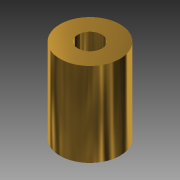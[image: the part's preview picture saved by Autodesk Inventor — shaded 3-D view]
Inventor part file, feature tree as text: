
AUTODESK INVENTOR PART (.ipt)
format: ipt  version: 2015 (Build 190159000, 159)  size: 105,984 bytes
history: native  units: mm
features: extrude x2, sketch x2, other x1
ambient origin geometry x8: Origin, YZ Plane, XZ Plane, XY Plane, X Axis, Y Axis, Z Axis, Center Point
bodies: Body1 (feature_tree)
feature tree (5):
  other  "ソリッド1"
  extrude  "押し出し1"  Depth=10.0mm
  extrude  "押し出し2"  Depth=14.0mm TaperAngle=0.0deg
  sketch  "スケッチ1"
  sketch  "スケッチ2"
